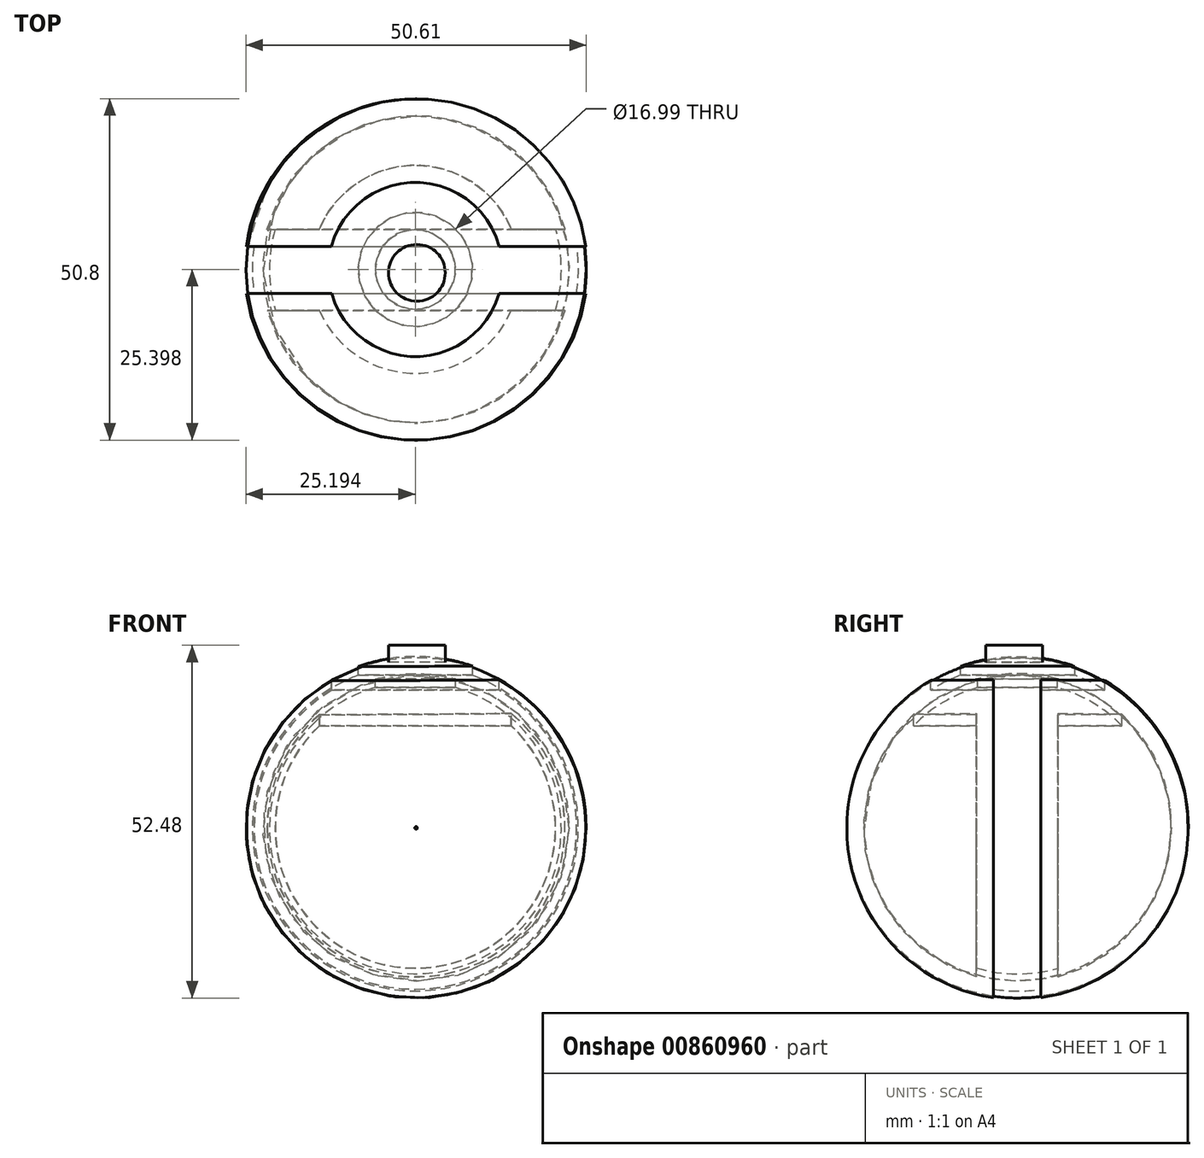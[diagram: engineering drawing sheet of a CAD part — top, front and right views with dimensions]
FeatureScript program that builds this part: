
annotation { "Feature Type Name" : "Feature", "Feature Type Description" : "" }
export const myFeature = defineFeature(function(context is Context, id is Id, definition is map)
    precondition{}
    {
        {
            var Q0;
            Q0=qCreatedBy(makeId("Top.planeOp"),FACE);
            var sketch = newSketch(context, id + "F0", { "sketchPlane" : qUnion([Q0])});
            skArc(sketch, "E0", {"start": v(-6.73, 3.15) * mm, "mid": v(-3.88, 6.49) * mm, "end": v(0.35, 7.7) * mm});
            skArc(sketch, "E1.0", {"start": v(0.35, 25.48) * mm, "mid": v(-25.15, 0.08) * mm, "end": v(0.35, -25.32) * mm});
            skLineSegment(sketch, "E2", {"start": v(-24.97, 3.15) * mm, "end": v(-6.73, 3.15) * mm});
            skLineSegment(sketch, "E3", {"start": v(-24.97, -2.92) * mm, "end": v(-6.76, -2.92) * mm});
            skLineSegment(sketch, "E4", {"start": v(25.46, 3.15) * mm, "end": v(25.47, 3.15) * mm});
            skArc(sketch, "E5.trimOffspring", {"start": v(0.35, -7.54) * mm, "mid": v(-3.9, -6.31) * mm, "end": v(-6.76, -2.92) * mm});
            skArc(sketch, "E6", {"start": v(0.35, 5.87) * mm, "mid": v(-5.54, 0.08) * mm, "end": v(0.35, -5.71) * mm});
            skLineSegment(sketch, "E7", {"start": v(0.35, 25.48) * mm, "end": v(0.35, -25.32) * mm});
            skPoint(sketch, "E8.orphan", {"position": v(7.22, 3.15) * mm});
            skPoint(sketch, "E9.end.orphan", {"position": v(25.47, -2.92) * mm});
            skPoint(sketch, "E10.orphan", {"position": v(7.25, -2.92) * mm});
            skSolve(sketch);
        }
        {
            var Q0;
            {var subQ3=sQuery(id+"F0.wireOp",EDGE,"E0");Q0=makeQuery(id+"F0.imprint","IMPRINT",FACE,{"disambiguationData":[TD([[makeQuery(id+"F0.imprint","IMPRINT",EDGE,{"derivedFrom":subQ3}),-1.0]])]});}
            var Q1;
            {var subQ0=sQuery(id+"F0.wireOp",EDGE,"E0");Q1=makeQuery(id+"F0.imprint","IMPRINT",FACE,{"disambiguationData":[TD([[makeQuery(id+"F0.imprint","IMPRINT",EDGE,{"derivedFrom":subQ0}),1.0]])]});}
            var Q2;
            {var subQ0=sQuery(id+"F0.wireOp",EDGE,"E6");Q2=makeQuery(id+"F0.imprint","IMPRINT",FACE,{"disambiguationData":[TD([[makeQuery(id+"F0.imprint","IMPRINT",EDGE,{"derivedFrom":subQ0}),1.0]])]});}
            var Q3;
            {var subQ3=sQuery(id+"F0.wireOp",EDGE,"E3");Q3=makeQuery(id+"F0.imprint","IMPRINT",FACE,{"disambiguationData":[TD([[makeQuery(id+"F0.imprint","IMPRINT",EDGE,{"derivedFrom":subQ3}),-1.0]])]});}
            var Q4;
            Q4=sQuery(id+"F0.wireOp",EDGE,"E7");
            revolve(context, id + "F1", {"surfaceOperationType" : NewSurfaceOperationType.NEW, "entities" : qUnion([Q0, Q1, Q2, Q3]), "axis" : qUnion([Q4]), "revolveType" : RevolveType.FULL});
        }
        {
            var Q0;
            Q0=qCreatedBy(makeId("Top.planeOp"),FACE);
            cPlane(context, id + "F2", {"entities" : qUnion([Q0]), "cplaneType" : CPlaneType.OFFSET, "offset" : 24.64 * mm, "width" : 152.4 * mm, "height" : 152.4 * mm});
        }
        {
            var Q0;
            Q0=qCreatedBy(id+"F2.planeOp",FACE);
            var sketch = newSketch(context, id + "F3", { "sketchPlane" : qUnion([Q0])});
            skArc(sketch, "E11", {"start": v(-12.22, -3.5) * mm, "mid": v(0.23, -12.88) * mm, "end": v(12.68, -3.5) * mm});
            skCircle(sketch, "E12", {"center": v(0.23, 0.08) * mm, "radius": 8.5 * mm});
            skCircle(sketch, "E13", {"center": v(0.23, 0.08) * mm, "radius": 2.96 * mm});
            skLineSegment(sketch, "E14", {"start": v(-27.68, 3.5) * mm, "end": v(-12.26, 3.5) * mm});
            skLineSegment(sketch, "E15.MirrorCS", {"start": v(-27.68, -3.5) * mm, "end": v(-12.26, -3.5) * mm});
            skLineSegment(sketch, "E16.MirrorCS", {"start": v(-12.26, -3.5) * mm, "end": v(-12.22, -3.5) * mm});
            skLineSegment(sketch, "E17.trimOffspring", {"start": v(12.68, -3.5) * mm, "end": v(26.74, -3.5) * mm});
            skLineSegment(sketch, "E18.trimOffspring", {"start": v(12.73, 3.5) * mm, "end": v(26.74, 3.5) * mm});
            skPoint(sketch, "E19.MirrorCS.start.orphan", {"position": v(-12.26, 3.5) * mm});
            skArc(sketch, "E20.trimOffspring", {"start": v(12.73, 3.5) * mm, "mid": v(0.23, 13.03) * mm, "end": v(-12.26, 3.5) * mm});
            skArc(sketch, "E21", {"start": v(-27.68, 3.5) * mm, "mid": v(-27.82, 0) * mm, "end": v(-27.68, -3.5) * mm});
            skArc(sketch, "E22", {"start": v(26.74, -3.5) * mm, "mid": v(27.02, 0) * mm, "end": v(26.74, 3.5) * mm});
            skSolve(sketch);
        }
        {
            var Q0;
            Q0=makeQuery(id+"F3.imprint","IMPRINT",FACE,{"disambiguationData":[TD([[makeQuery(id+"F3.imprint","IMPRINT",EDGE,{"derivedFrom":sQuery(id+"F3.wireOp",EDGE,"E11")}),1.0]])]});
            extrude(context, id + "F4", {"entities" : qUnion([Q0]), "operationType" : NewBodyOperationType.REMOVE, "oppositeDirection" : true, "depth" : 39.37 * mm, "offsetDistance" : 25.4 * mm});
        }
        {
            var Q0;
            Q0=qCreatedBy(makeId("Top.planeOp"),FACE);
            var sketch = newSketch(context, id + "F5", { "sketchPlane" : qUnion([Q0])});
            skArc(sketch, "E23", {"start": v(-0.08, 24) * mm, "mid": v(-24, -0.16) * mm, "end": v(0.07, -24.15) * mm});
            skLineSegment(sketch, "E24", {"start": v(-0.08, 24) * mm, "end": v(0.07, -24.15) * mm});
            skLineSegment(sketch, "E25", {"start": v(-11.07, 4.18) * mm, "end": v(-11.6, 4.17) * mm});
            skSolve(sketch);
        }
        {
            var Q0;
            Q0=makeQuery(id+"F5.imprint","IMPRINT",FACE,{"disambiguationData":[TD([[makeQuery(id+"F5.imprint","IMPRINT",EDGE,{"derivedFrom":sQuery(id+"F5.wireOp",EDGE,"E23")}),1.0]])]});
            var Q1;
            Q1=sQuery(id+"F5.wireOp",EDGE,"E24");
            revolve(context, id + "F6", {"operationType" : NewBodyOperationType.ADD, "surfaceOperationType" : NewSurfaceOperationType.NEW, "entities" : qUnion([Q0]), "axis" : qUnion([Q1]), "revolveType" : RevolveType.FULL});
        }
        {
            var Q0;
            Q0=qCreatedBy(id+"F2.planeOp",FACE);
            var sketch = newSketch(context, id + "F7", { "sketchPlane" : qUnion([Q0])});
            skCircle(sketch, "E26", {"center": v(-48.81, 31.08) * mm, "radius": 4.22 * mm});
            skArc(sketch, "E27", {"start": v(-8.03, -1.89) * mm, "mid": v(-7.8, -2.71) * mm, "end": v(-7.47, -3.5) * mm});
            skSolve(sketch);
        }
        {
            var Q0;
            Q0=makeQuery(id+"F7.imprint","IMPRINT",FACE,{"disambiguationData":[TD([[makeQuery(id+"F7.imprint","IMPRINT",EDGE,{"derivedFrom":sQuery(id+"F7.wireOp",EDGE,"E26")}),1.0]])]});
            extrude(context, id + "F8", {"entities" : qUnion([Q0]), "depth" : 2.54 * mm, "offsetDistance" : 25.4 * mm});
        }
        {
            var Q0;
            Q0=makeQuery(id+"F8.opExtrude","SWEPT_BODY",BODY,{"disambiguationData":[OSD([sQuery(id+"F7.wireOp",EDGE,"E26")])]});
            transform(context, id + "F9", {"entities" : qUnion([Q0]), "transformType" : TransformType.TRANSLATION_3D, "dx" : 49.28 * mm, "dy" : -31.5 * mm, "dz" : 0 * mm, "makeCopy" : false});
        }
        {
            var Q0;
            Q0=qCreatedBy(makeId("Top.planeOp"),FACE);
            var sketch = newSketch(context, id + "F10", { "sketchPlane" : qUnion([Q0])});
            skLineSegment(sketch, "E28", {"start": v(-20.15, -3.5) * mm, "end": v(20.85, -3.5) * mm});
            skLineSegment(sketch, "E29", {"start": v(-20.18, 3.5) * mm, "end": v(20.87, 3.5) * mm});
            skArc(sketch, "E30", {"start": v(-20.18, 3.5) * mm, "mid": v(-20.66, 0) * mm, "end": v(-20.15, -3.5) * mm});
            skArc(sketch, "E31", {"start": v(20.85, -3.5) * mm, "mid": v(21.3, 0) * mm, "end": v(20.87, 3.5) * mm});
            skSolve(sketch);
        }
        {
            var Q0;
            Q0 = qSketchRegion(id + "F10", true);
            extrude(context, id + "F11", {"entities" : qUnion([Q0]), "operationType" : NewBodyOperationType.REMOVE, "oppositeDirection" : true, "depth" : 32 * mm, "offsetDistance" : 25.4 * mm});
        }
        {
            var Q0;
            Q0=qCreatedBy(makeId("Top.planeOp"),FACE);
            var sketch = newSketch(context, id + "F12", { "sketchPlane" : qUnion([Q0])});
            skArc(sketch, "E32", {"start": v(0.23, 24.33) * mm, "mid": v(-24.02, 0.08) * mm, "end": v(0.23, -24.17) * mm});
            skLineSegment(sketch, "E33", {"start": v(0.23, 24.33) * mm, "end": v(0.23, -24.17) * mm});
            skSolve(sketch);
        }
        {
            var Q0;
            Q0 = qSketchRegion(id + "F12", true);
            var Q1;
            Q1=sQuery(id+"F12.wireOp",EDGE,"E33");
            revolve(context, id + "F13", {"operationType" : NewBodyOperationType.ADD, "surfaceOperationType" : NewSurfaceOperationType.NEW, "entities" : qUnion([Q0]), "axis" : qUnion([Q1]), "revolveType" : RevolveType.FULL});
        }
        {
            var Q0;
            {var subQ0=sQuery(id+"F3.wireOp",EDGE,"E14");var subQ1=makeQuery(id+"F4.opExtrude","SWEPT_FACE",FACE,{"disambiguationData":[OSD([subQ0])]});var subQ9=sQuery(id+"F3.wireOp",EDGE,"E11");Q0=makeQuery(id+"F11.boolean.opBoolean","SPLIT",FACE,{"disambiguationData":[TD([makeQuery(id+"F4.boolean.opBoolean","COPY",FACE,{"derivedFrom":subQ1})])],"derivedFrom":makeQuery(id+"F4.boolean.opBoolean","SPLIT",FACE,{"disambiguationData":[TD([makeQuery(id+"F4.opExtrude","SWEPT_FACE",FACE,{"disambiguationData":[OSD([subQ9])]})])],"derivedFrom":makeQuery(id+"F1.opRevolve","SWEPT_FACE",FACE,{"disambiguationData":[OSD([sQuery(id+"F0.wireOp",EDGE,"E1.0")])]})})});}
            var Q1;
            Q1=makeQuery(id+"F1.opRevolve","SWEPT_BODY",BODY,{"disambiguationData":[OSD([sQuery(id+"F0.wireOp",EDGE,"E1.0"),sQuery(id+"F0.wireOp",EDGE,"E7")])]});
            shell(context, id + "F14", {"isHollow" : true, "entities" : qUnion([Q0]), "parts" : qUnion([Q1]), "thickness" : 2.54 * mm});
        }
    });
